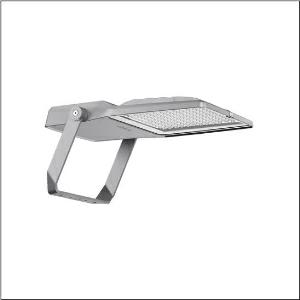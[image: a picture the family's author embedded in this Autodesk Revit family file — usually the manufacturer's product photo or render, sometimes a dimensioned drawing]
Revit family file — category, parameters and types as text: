
# Revit family: floodlight_fl_21_iq_midi___rs12_5xa7782f5b1a_9a70
name_source: partatom
category: Lighting Fixtures
units: mm (PartAtom-declared; Revit-internal decimal feet)

## family parameters
Cut with Voids When Loaded = No
Host = Face
Light Source = No
Part Type = Normal
Room Calculation Point = No
Round Connector Dimension = Use Diameter
Shared = No

## types (1)
- --- (1 x LED, 33220 lm, 270.2 W, 4000K)
    Apparent Load = 270 VA
    CIE Flux Codes = 79 92 99 100 100
    Color Rendering = 80
    Color Temperature = 4000K
    Default Elevation = 1800 mm
    Description = Floodlight FL 21 iQ midi, floodlight, primary light control with lens, of PMMA, primary optical cover: protective disc, of toughened safety glass, transparent, light distribution: RS12, light emission: direct distribution, installation type: surface-mounted, LED, High Power LED, rated luminous flux: 33.220lm, luminous efficacy: 123lm/W, light colour: 840, colour temperature: 4000K, control gear: ECG iQ, control: optimised constant luminous flux control (CLO 2.0), Desk-Remote (wireless, voltage-free reading and setting of iQ features in the workshop via application-optimized NFC function/RFID function), Smart-Wire, Night-Set, Temp-Guard, Street-Remote, Auto-Match, with terminal, 6-pole, mains connection: 220..240V, AC, 50/60Hz, start of lifetime: 270W, end of service life: 287W, reduction: 118W, luminaire housing, of diecast aluminium, powder-coated, Siteco® metallic grey (DB 702S), corrosivity category C5 mid according to DIN EN ISO 12944, sealing non-destructively replaceable, mounting bracket, of steel, galvanised, powder-coated, Siteco® metallic grey (DB 702S), protection rating (complete): IP66, insulation class (complete): insulation class II (safety insulation), certification: CE, protection symbol: D, impact resistance: IK08, permissible operating ambient temperature: -40..+40°C, permissible operating ambient temperature for outdoor applications: -40..+50°C, standard: DIN EN 12944, LABS conformity tested according to VDMA 24364:2018-05, packaging unit: 1 piece

Light Distribution: RS12
    Height = 76 mm
    Lamp = 1 x LED
    Lamp Light Flux = 33220 lm
    Lamp Power = 270.2 W
    Lamp count = 1
    Length = 657 mm
    Luminous efficacy = 123 lm/W
    Manufacturer = Siteco
    ModVariant = No
    Model = 5XA7782F5B1A
    Number of Poles = 1
    OnlyDefault = Yes
    Power Factor = 1
    Product Name = Floodlight FL 21 iQ midi | RS12
    Product group = floodlight | pylon annexe
    ProductGroupID = 6200
    Protection Class = Protection class II
    Protection Degree = IP 66
    RLX_Detail_Level = 1
    RLX_Emergency_Light_Flux = 0 lm
    RLX_Emergency_Type = 0
    RLX_Emergency_Type_DB = No
    RlxData = <blob elided: 141349 chars, md5=9946cba1>
    Socket = socket
    Standby Power = 0 W
    System Light Flux = 33220 lm
    System Power = 270 W
    Type Comments = factory setting: luminous flux: 100 % | dim-lin: 254 | 620 mA
    Type Image = l_1006876.jpg
    URL = http://relux.com
    VarID = @adj_037527
    Voltage = 0 V
    Weight = 0.00 kg
    Width = 442 mm

## geometry (parser evidence)
native form markers: Blend x4, Sweep x12
no freeform markers — native parametric forms only
